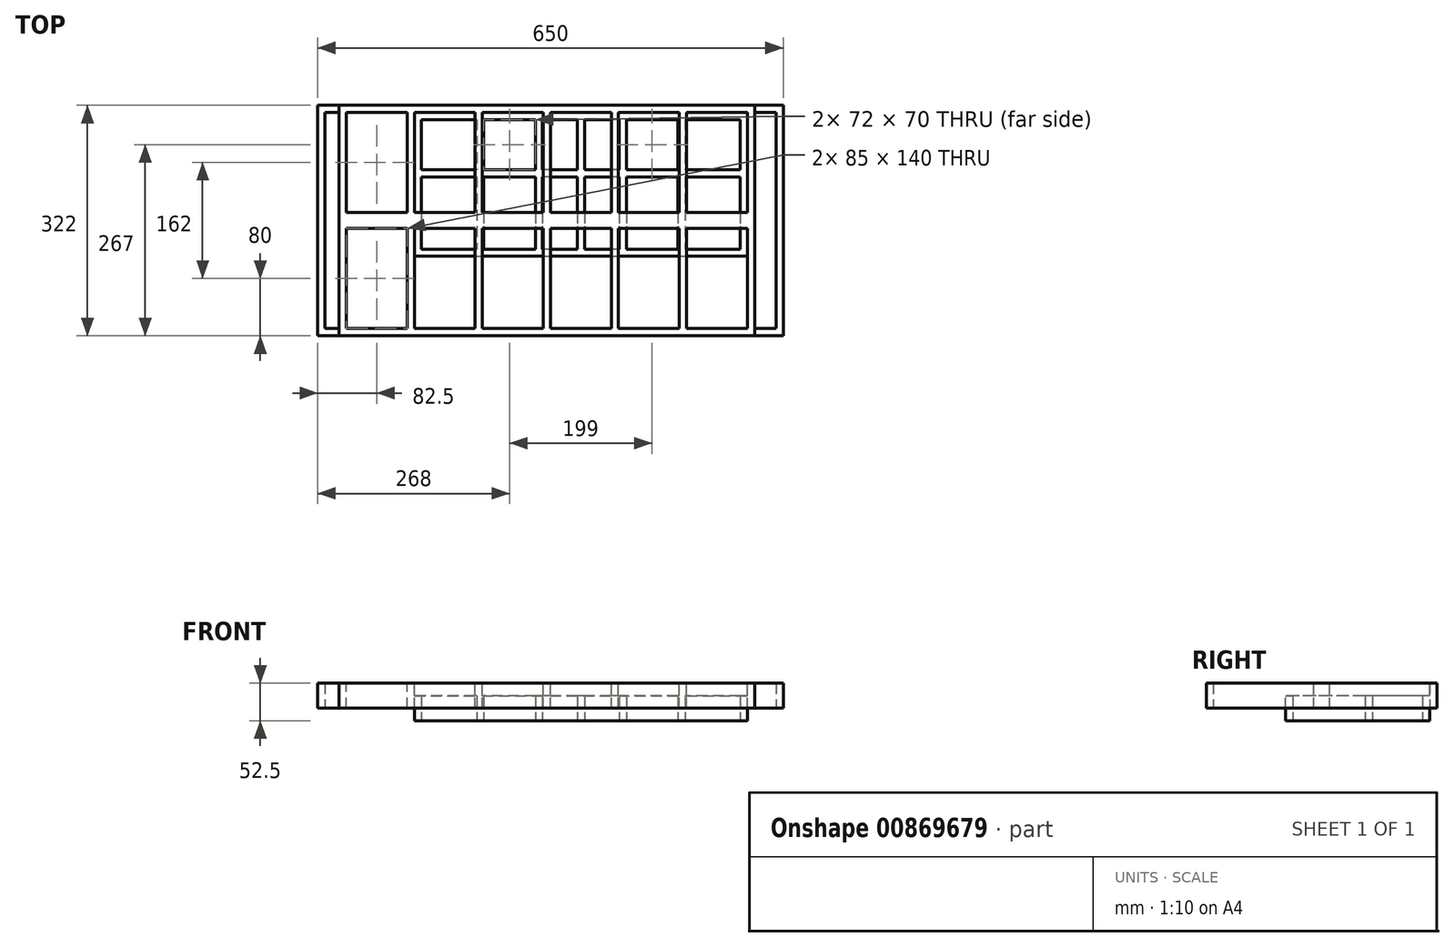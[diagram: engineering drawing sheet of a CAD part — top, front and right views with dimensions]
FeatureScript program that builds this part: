
annotation { "Feature Type Name" : "Feature", "Feature Type Description" : "" }
export const myFeature = defineFeature(function(context is Context, id is Id, definition is map)
    precondition{}
    {
        {
            var Q0;
            Q0=qCreatedBy(makeId("Top.planeOp"),FACE);
            var sketch = newSketch(context, id + "F0", { "sketchPlane" : qUnion([Q0])});
            skLineSegment(sketch, "E0.bottom", {"start": v(-290, 161) * mm, "end": v(290, 161) * mm});
            skLineSegment(sketch, "E0.top", {"start": v(-290, -161) * mm, "end": v(290, -161) * mm});
            skLineSegment(sketch, "E0.left", {"start": v(-290, 161) * mm, "end": v(-290, -161) * mm});
            skLineSegment(sketch, "E0.right", {"start": v(290, 161) * mm, "end": v(290, -161) * mm});
            skPoint(sketch, "E0.middle", {"position": v(0, 0) * mm});
            skSolve(sketch);
        }
        {
            var Q0;
            Q0 = qSketchRegion(id + "F0", true);
            extrude(context, id + "F1", {"entities" : qUnion([Q0]), "depth" : 35 * mm, "offsetDistance" : 25 * mm, "symmetric" : true});
        }
        {
            var Q0;
            Q0=qCreatedBy(makeId("Top.planeOp"),FACE);
            var sketch = newSketch(context, id + "F2", { "sketchPlane" : qUnion([Q0])});
            skLineSegment(sketch, "E1.bottom", {"start": v(195, -11) * mm, "end": v(280, -11) * mm});
            skLineSegment(sketch, "E1.top", {"start": v(195, -151) * mm, "end": v(280, -151) * mm});
            skLineSegment(sketch, "E1.left", {"start": v(195, -11) * mm, "end": v(195, -151) * mm});
            skLineSegment(sketch, "E1.right", {"start": v(280, -11) * mm, "end": v(280, -151) * mm});
            skLineSegment(sketch, "E2.1.0.0", {"start": v(100, -11) * mm, "end": v(185, -11) * mm});
            skLineSegment(sketch, "E2.1.0.1", {"start": v(100, -11) * mm, "end": v(100, -151) * mm});
            skLineSegment(sketch, "E2.1.0.2", {"start": v(185, -11) * mm, "end": v(185, -151) * mm});
            skLineSegment(sketch, "E2.1.0.3", {"start": v(100, -151) * mm, "end": v(185, -151) * mm});
            skLineSegment(sketch, "E2.2.0.0", {"start": v(5, -11) * mm, "end": v(90, -11) * mm});
            skLineSegment(sketch, "E2.2.0.1", {"start": v(5, -11) * mm, "end": v(5, -151) * mm});
            skLineSegment(sketch, "E2.2.0.2", {"start": v(90, -11) * mm, "end": v(90, -151) * mm});
            skLineSegment(sketch, "E2.2.0.3", {"start": v(5, -151) * mm, "end": v(90, -151) * mm});
            skLineSegment(sketch, "E2.3.0.0", {"start": v(-90, -11) * mm, "end": v(-5, -11) * mm});
            skLineSegment(sketch, "E2.3.0.1", {"start": v(-90, -11) * mm, "end": v(-90, -151) * mm});
            skLineSegment(sketch, "E2.3.0.2", {"start": v(-5, -11) * mm, "end": v(-5, -151) * mm});
            skLineSegment(sketch, "E2.3.0.3", {"start": v(-90, -151) * mm, "end": v(-5, -151) * mm});
            skLineSegment(sketch, "E2.4.0.0", {"start": v(-185, -11) * mm, "end": v(-100, -11) * mm});
            skLineSegment(sketch, "E2.4.0.1", {"start": v(-185, -11) * mm, "end": v(-185, -151) * mm});
            skLineSegment(sketch, "E2.4.0.2", {"start": v(-100, -11) * mm, "end": v(-100, -151) * mm});
            skLineSegment(sketch, "E2.4.0.3", {"start": v(-185, -151) * mm, "end": v(-100, -151) * mm});
            skLineSegment(sketch, "E2.direction1", {"start": v(195, -151) * mm, "end": v(100, -151) * mm, "construction": true});
            skLineSegment(sketch, "E3", {"start": v(-290, 0) * mm, "end": v(290, 0) * mm, "construction": true});
            skLineSegment(sketch, "E4.MirrorCS", {"start": v(100, 151) * mm, "end": v(185, 151) * mm});
            skLineSegment(sketch, "E5.MirrorCS", {"start": v(280, 11) * mm, "end": v(280, 151) * mm});
            skLineSegment(sketch, "E6.MirrorCS", {"start": v(5, 11) * mm, "end": v(5, 151) * mm});
            skLineSegment(sketch, "E7.MirrorCS", {"start": v(-185, 11) * mm, "end": v(-100, 11) * mm});
            skLineSegment(sketch, "E8.MirrorCS", {"start": v(-185, 11) * mm, "end": v(-185, 151) * mm});
            skLineSegment(sketch, "E9.MirrorCS", {"start": v(195, 151) * mm, "end": v(280, 151) * mm});
            skLineSegment(sketch, "E10.MirrorCS", {"start": v(-100, 11) * mm, "end": v(-100, 151) * mm});
            skLineSegment(sketch, "E11.MirrorCS", {"start": v(100, 11) * mm, "end": v(185, 11) * mm});
            skLineSegment(sketch, "E12.MirrorCS", {"start": v(185, 11) * mm, "end": v(185, 151) * mm});
            skLineSegment(sketch, "E13.MirrorCS", {"start": v(195, 11) * mm, "end": v(280, 11) * mm});
            skLineSegment(sketch, "E14.MirrorCS", {"start": v(-90, 11) * mm, "end": v(-90, 151) * mm});
            skLineSegment(sketch, "E15.MirrorCS", {"start": v(90, 11) * mm, "end": v(90, 151) * mm});
            skLineSegment(sketch, "E16.MirrorCS", {"start": v(195, 151) * mm, "end": v(100, 151) * mm, "construction": true});
            skLineSegment(sketch, "E17.MirrorCS", {"start": v(100, 11) * mm, "end": v(100, 151) * mm});
            skLineSegment(sketch, "E18.MirrorCS", {"start": v(-90, 11) * mm, "end": v(-5, 11) * mm});
            skLineSegment(sketch, "E19.MirrorCS", {"start": v(-185, 151) * mm, "end": v(-100, 151) * mm});
            skLineSegment(sketch, "E20.MirrorCS", {"start": v(5, 11) * mm, "end": v(90, 11) * mm});
            skLineSegment(sketch, "E21.MirrorCS", {"start": v(-5, 11) * mm, "end": v(-5, 151) * mm});
            skLineSegment(sketch, "E22.MirrorCS", {"start": v(195, 11) * mm, "end": v(195, 151) * mm});
            skLineSegment(sketch, "E23.MirrorCS", {"start": v(-90, 151) * mm, "end": v(-5, 151) * mm});
            skLineSegment(sketch, "E24.MirrorCS", {"start": v(5, 151) * mm, "end": v(90, 151) * mm});
            skLineSegment(sketch, "E25", {"start": v(-280, 161) * mm, "end": v(-280, -161) * mm, "construction": true});
            skLineSegment(sketch, "E26.bottom", {"start": v(-280, 151) * mm, "end": v(-195, 151) * mm});
            skLineSegment(sketch, "E26.top", {"start": v(-280, 11) * mm, "end": v(-195, 11) * mm});
            skLineSegment(sketch, "E26.left", {"start": v(-280, 151) * mm, "end": v(-280, 11) * mm});
            skLineSegment(sketch, "E26.right", {"start": v(-195, 151) * mm, "end": v(-195, 11) * mm});
            skLineSegment(sketch, "E27.bottom", {"start": v(-280, -11) * mm, "end": v(-195, -11) * mm});
            skLineSegment(sketch, "E27.top", {"start": v(-280, -151) * mm, "end": v(-195, -151) * mm});
            skLineSegment(sketch, "E27.left", {"start": v(-280, -11) * mm, "end": v(-280, -151) * mm});
            skLineSegment(sketch, "E27.right", {"start": v(-195, -11) * mm, "end": v(-195, -151) * mm});
            skLineSegment(sketch, "E28", {"start": v(-185, 151) * mm, "end": v(-290, 151) * mm, "construction": true});
            skLineSegment(sketch, "E29", {"start": v(-185, -151) * mm, "end": v(-290, -151) * mm, "construction": true});
            skLineSegment(sketch, "E30", {"start": v(-195, 151) * mm, "end": v(-195, -151) * mm, "construction": true});
            skPoint(sketch, "E31", {"position": v(-280, 151) * mm});
            skPoint(sketch, "E32", {"position": v(-280, -151) * mm});
            skLineSegment(sketch, "E33", {"start": v(-290, 11) * mm, "end": v(-195, 11) * mm, "construction": true});
            skLineSegment(sketch, "E34", {"start": v(-290, -11) * mm, "end": v(-195, -11) * mm, "construction": true});
            skPoint(sketch, "E35", {"position": v(-280, -11) * mm});
            skSolve(sketch);
        }
        {
            var Q0;
            Q0 = qSketchRegion(id + "F2", true);
            extrude(context, id + "F3", {"entities" : qUnion([Q0]), "operationType" : NewBodyOperationType.REMOVE, "oppositeDirection" : true, "depth" : 50 * mm, "offsetDistance" : 25 * mm, "symmetric" : true});
        }
        {
            var Q0;
            Q0=qCreatedBy(makeId("Top.planeOp"),FACE);
            var sketch = newSketch(context, id + "F4", { "sketchPlane" : qUnion([Q0])});
            skLineSegment(sketch, "E36.bottom", {"start": v(-185, 151) * mm, "end": v(280, 151) * mm});
            skLineSegment(sketch, "E36.top", {"start": v(-185, -50) * mm, "end": v(280, -50) * mm});
            skLineSegment(sketch, "E36.left", {"start": v(-185, 151) * mm, "end": v(-185, -50) * mm});
            skLineSegment(sketch, "E36.right", {"start": v(280, 151) * mm, "end": v(280, -50) * mm});
            skLineSegment(sketch, "E37.bottom", {"start": v(280, 151) * mm, "end": v(-185, 151) * mm});
            skLineSegment(sketch, "E37.top", {"start": v(280, -50) * mm, "end": v(-185, -50) * mm});
            skLineSegment(sketch, "E37.left", {"start": v(280, 120) * mm, "end": v(280, -50) * mm});
            skLineSegment(sketch, "E38", {"start": v(280, 151) * mm, "end": v(280, 151) * mm});
            skSolve(sketch);
        }
        {
            var Q0;
            Q0 = qSketchRegion(id + "F4", true);
            extrude(context, id + "F5", {"entities" : qUnion([Q0]), "operationType" : NewBodyOperationType.ADD, "oppositeDirection" : true, "depth" : 35 * mm, "offsetDistance" : 25 * mm});
        }
        {
            var Q0;
            Q0=makeQuery(id+"F5.opExtrude","CAP_FACE",FACE,{"disambiguationData":[OSD([sQuery(id+"F4.wireOp",EDGE,"E37.bottom"),sQuery(id+"F4.wireOp",EDGE,"E37.top"),sQuery(id+"F4.wireOp",EDGE,"E37.left"),sQuery(id+"F4.wireOp",EDGE,"E36.left")])],"isStart":false});
            var sketch = newSketch(context, id + "F6", { "sketchPlane" : qUnion([Q0])});
            skLineSegment(sketch, "E39.bottom", {"start": v(270, -141) * mm, "end": v(193, -141) * mm});
            skLineSegment(sketch, "E39.top", {"start": v(270, 40) * mm, "end": v(193, 40) * mm});
            skLineSegment(sketch, "E39.left", {"start": v(270, -141) * mm, "end": v(270, -71) * mm});
            skLineSegment(sketch, "E39.right", {"start": v(-175, -141) * mm, "end": v(-175, -71) * mm});
            skLineSegment(sketch, "E40", {"start": v(106, -141) * mm, "end": v(106, 40) * mm, "construction": true});
            skLineSegment(sketch, "E41", {"start": v(-11, -141) * mm, "end": v(-11, 40) * mm, "construction": true});
            skLineSegment(sketch, "E42", {"start": v(47.5, -141) * mm, "end": v(47.5, 40) * mm, "construction": true});
            skLineSegment(sketch, "E43", {"start": v(188, -141) * mm, "end": v(188, 40) * mm, "construction": true});
            skLineSegment(sketch, "E44", {"start": v(193, -141) * mm, "end": v(193, -71) * mm});
            skLineSegment(sketch, "E45.MirrorCS", {"start": v(183, -141) * mm, "end": v(183, -71) * mm});
            skLineSegment(sketch, "E46", {"start": v(111, -141) * mm, "end": v(111, -71) * mm});
            skLineSegment(sketch, "E47", {"start": v(52.5, -141) * mm, "end": v(52.5, -71) * mm});
            skLineSegment(sketch, "E48", {"start": v(-98, -141) * mm, "end": v(-98, -71) * mm});
            skLineSegment(sketch, "E49", {"start": v(-16, -141) * mm, "end": v(-16, -71) * mm});
            skLineSegment(sketch, "E50.MirrorCS", {"start": v(-88, -141) * mm, "end": v(-88, -71) * mm});
            skLineSegment(sketch, "E51.MirrorCS", {"start": v(-6, -141) * mm, "end": v(-6, -71) * mm});
            skLineSegment(sketch, "E52.MirrorCS", {"start": v(42.5, -141) * mm, "end": v(42.5, -71) * mm});
            skLineSegment(sketch, "E53.MirrorCS", {"start": v(101, -141) * mm, "end": v(101, -71) * mm});
            skLineSegment(sketch, "E54.trimOffspring", {"start": v(183, -141) * mm, "end": v(111, -141) * mm});
            skLineSegment(sketch, "E55.trimOffspring", {"start": v(101, -141) * mm, "end": v(52.5, -141) * mm});
            skLineSegment(sketch, "E56.trimOffspring", {"start": v(42.5, -141) * mm, "end": v(-6, -141) * mm});
            skLineSegment(sketch, "E57.trimOffspring", {"start": v(-16, -141) * mm, "end": v(-88, -141) * mm});
            skLineSegment(sketch, "E58.trimOffspring", {"start": v(183, 40) * mm, "end": v(111, 40) * mm});
            skLineSegment(sketch, "E59.trimOffspring", {"start": v(101, 40) * mm, "end": v(52.5, 40) * mm});
            skLineSegment(sketch, "E60.trimOffspring", {"start": v(42.5, 40) * mm, "end": v(-6, 40) * mm});
            skLineSegment(sketch, "E61.trimOffspring", {"start": v(-16, 40) * mm, "end": v(-88, 40) * mm});
            skLineSegment(sketch, "E62.trimOffspring", {"start": v(-98, -141) * mm, "end": v(-175, -141) * mm});
            skLineSegment(sketch, "E63.trimOffspring", {"start": v(-98, 40) * mm, "end": v(-175, 40) * mm});
            skLineSegment(sketch, "E64", {"start": v(270, -71) * mm, "end": v(193, -71) * mm});
            skLineSegment(sketch, "E65.MirrorCS", {"start": v(270, -61) * mm, "end": v(193, -61) * mm});
            skLineSegment(sketch, "E66.trimOffspring", {"start": v(270, -61) * mm, "end": v(270, 40) * mm});
            skLineSegment(sketch, "E67.trimOffspring", {"start": v(193, -61) * mm, "end": v(193, 40) * mm});
            skLineSegment(sketch, "E68.trimOffspring", {"start": v(183, -71) * mm, "end": v(111, -71) * mm});
            skLineSegment(sketch, "E69.trimOffspring", {"start": v(183, -61) * mm, "end": v(183, 40) * mm});
            skLineSegment(sketch, "E70.trimOffspring", {"start": v(111, -61) * mm, "end": v(111, 40) * mm});
            skLineSegment(sketch, "E71.trimOffspring", {"start": v(101, -71) * mm, "end": v(52.5, -71) * mm});
            skLineSegment(sketch, "E72.trimOffspring", {"start": v(101, -61) * mm, "end": v(101, 40) * mm});
            skLineSegment(sketch, "E73.trimOffspring", {"start": v(52.5, -61) * mm, "end": v(52.5, 40) * mm});
            skLineSegment(sketch, "E74.trimOffspring", {"start": v(42.5, -71) * mm, "end": v(-6, -71) * mm});
            skLineSegment(sketch, "E75.trimOffspring", {"start": v(42.5, -61) * mm, "end": v(-6, -61) * mm});
            skLineSegment(sketch, "E76.trimOffspring", {"start": v(42.5, -61) * mm, "end": v(42.5, 40) * mm});
            skLineSegment(sketch, "E77.trimOffspring", {"start": v(-6, -61) * mm, "end": v(-6, 40) * mm});
            skLineSegment(sketch, "E78.trimOffspring", {"start": v(-16, -71) * mm, "end": v(-88, -71) * mm});
            skLineSegment(sketch, "E79.trimOffspring", {"start": v(-16, -61) * mm, "end": v(-16, 40) * mm});
            skLineSegment(sketch, "E80.trimOffspring", {"start": v(-16, -61) * mm, "end": v(-88, -61) * mm});
            skLineSegment(sketch, "E81.trimOffspring", {"start": v(-98, -61) * mm, "end": v(-98, 40) * mm});
            skLineSegment(sketch, "E82.trimOffspring", {"start": v(-98, -71) * mm, "end": v(-175, -71) * mm});
            skLineSegment(sketch, "E83.trimOffspring", {"start": v(-88, -61) * mm, "end": v(-88, 40) * mm});
            skLineSegment(sketch, "E84.trimOffspring", {"start": v(-98, -61) * mm, "end": v(-175, -61) * mm});
            skLineSegment(sketch, "E85.trimOffspring", {"start": v(-175, -61) * mm, "end": v(-175, 40) * mm});
            skLineSegment(sketch, "E86.trimOffspring", {"start": v(183, -61) * mm, "end": v(111, -61) * mm});
            skLineSegment(sketch, "E87.trimOffspring", {"start": v(101, -61) * mm, "end": v(52.5, -61) * mm});
            skSolve(sketch);
        }
        {
            var Q0;
            Q0 = qSketchRegion(id + "F6", true);
            extrude(context, id + "F7", {"entities" : qUnion([Q0]), "operationType" : NewBodyOperationType.REMOVE, "oppositeDirection" : true, "depth" : 35 * mm, "offsetDistance" : 25 * mm});
        }
        {
            var Q0;
            Q0=makeQuery(id+"F1.opExtrude","SWEPT_FACE",FACE,{"disambiguationData":[OSD([sQuery(id+"F0.wireOp",EDGE,"E0.left")])]});
            var sketch = newSketch(context, id + "F8", { "sketchPlane" : qUnion([Q0])});
            skLineSegment(sketch, "E88.bottom", {"start": v(-161, -17.5) * mm, "end": v(161, -17.5) * mm});
            skLineSegment(sketch, "E88.top", {"start": v(-161, 17.5) * mm, "end": v(161, 17.5) * mm});
            skLineSegment(sketch, "E88.left", {"start": v(-161, -17.5) * mm, "end": v(-161, 17.5) * mm});
            skLineSegment(sketch, "E88.right", {"start": v(161, -17.5) * mm, "end": v(161, 17.5) * mm});
            skPoint(sketch, "E88.middle", {"position": v(0, 0) * mm});
            skSolve(sketch);
        }
        {
            var Q0;
            Q0 = qSketchRegion(id + "F8", true);
            extrude(context, id + "F9", {"entities" : qUnion([Q0]), "depth" : 30 * mm, "offsetDistance" : 25 * mm});
        }
        {
            var Q0;
            Q0=makeQuery(id+"F9.opExtrude","SWEPT_FACE",FACE,{"disambiguationData":[OSD([sQuery(id+"F8.wireOp",EDGE,"E88.bottom")])]});
            var sketch = newSketch(context, id + "F10", { "sketchPlane" : qUnion([Q0])});
            skLineSegment(sketch, "E89.bottom", {"start": v(-290, -151) * mm, "end": v(-310, -151) * mm});
            skLineSegment(sketch, "E89.top", {"start": v(-290, 151) * mm, "end": v(-310, 151) * mm});
            skLineSegment(sketch, "E89.left", {"start": v(-290, -151) * mm, "end": v(-290, 151) * mm});
            skLineSegment(sketch, "E89.right", {"start": v(-310, -151) * mm, "end": v(-310, 151) * mm});
            skSolve(sketch);
        }
        {
            var Q0;
            Q0 = qSketchRegion(id + "F10", true);
            extrude(context, id + "F11", {"entities" : qUnion([Q0]), "operationType" : NewBodyOperationType.REMOVE, "endBound" : BoundingType.THROUGH_ALL, "oppositeDirection" : true, "depth" : 25 * mm, "offsetDistance" : 25 * mm});
        }
        {
            var Q0;
            Q0=makeQuery(id+"F1.opExtrude","SWEPT_FACE",FACE,{"disambiguationData":[OSD([sQuery(id+"F0.wireOp",EDGE,"E0.right")])]});
            var sketch = newSketch(context, id + "F12", { "sketchPlane" : qUnion([Q0])});
            skLineSegment(sketch, "E90.bottom", {"start": v(-161, 17.5) * mm, "end": v(161, 17.5) * mm});
            skLineSegment(sketch, "E90.top", {"start": v(-161, -17.5) * mm, "end": v(161, -17.5) * mm});
            skLineSegment(sketch, "E90.left", {"start": v(-161, 17.5) * mm, "end": v(-161, -17.5) * mm});
            skLineSegment(sketch, "E90.right", {"start": v(161, 17.5) * mm, "end": v(161, -17.5) * mm});
            skPoint(sketch, "E90.middle", {"position": v(0, 0) * mm});
            skSolve(sketch);
        }
        {
            var Q0;
            Q0 = qSketchRegion(id + "F12", true);
            extrude(context, id + "F13", {"entities" : qUnion([Q0]), "depth" : 40 * mm, "offsetDistance" : 25 * mm});
        }
        {
            var Q0;
            Q0=makeQuery(id+"F13.opExtrude","SWEPT_FACE",FACE,{"disambiguationData":[OSD([sQuery(id+"F12.wireOp",EDGE,"E90.top")])]});
            var sketch = newSketch(context, id + "F14", { "sketchPlane" : qUnion([Q0])});
            skLineSegment(sketch, "E91", {"start": v(290, 151) * mm, "end": v(320, 151) * mm});
            skLineSegment(sketch, "E92", {"start": v(320, 151) * mm, "end": v(320, -151) * mm});
            skLineSegment(sketch, "E93", {"start": v(320, -151) * mm, "end": v(290, -151) * mm});
            skSolve(sketch);
        }
        {
            var Q0;
            Q0 = qSketchRegion(id + "F14", true);
            var Q1;
            {var subQ0=sQuery(id+"F14.wireOp",EDGE,"E91");Q1=makeQuery(id+"F14.imprint","IMPRINT",FACE,{"disambiguationData":[TD([[makeQuery(id+"F14.imprint","IMPRINT",EDGE,{"derivedFrom":subQ0}),-1.0]])]});}
            extrude(context, id + "F15", {"entities" : qUnion([Q0, Q1]), "operationType" : NewBodyOperationType.REMOVE, "endBound" : BoundingType.THROUGH_ALL, "oppositeDirection" : true, "depth" : 25 * mm, "offsetDistance" : 25 * mm});
        }
    });
